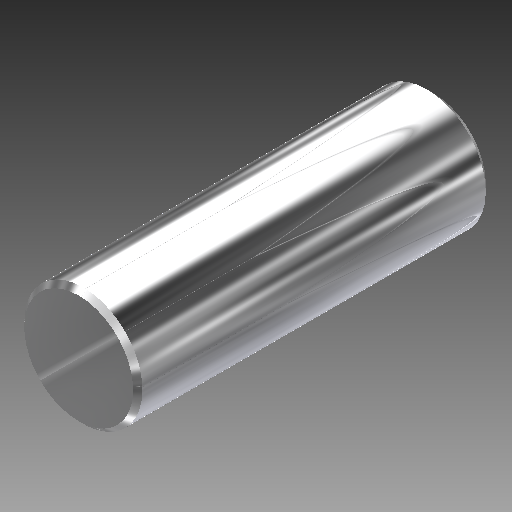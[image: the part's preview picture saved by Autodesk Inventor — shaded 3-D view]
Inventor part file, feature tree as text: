
AUTODESK INVENTOR PART (.ipt)
format: ipt  version: 2017 (Build 210142000, 142)  size: 182,784 bytes
history: native  units: in
note: dims shown in document units (in); Inventor stores cm internally (conversion verified against a paired STEP export)
features: other x35, revolve x1, sketch x1
ambient origin geometry x8: Origin, YZ Plane, XZ Plane, XY Plane, X Axis, Y Axis, Z Axis, Center Point
bodies: Solid1 (feature_tree)
feature tree (37):
  revolve  "Revolution1"  [1 undecoded]
  other  "dia1_XY"
  other  "dia1_YZ"
  other  "dia1_ZX"
  other  "dia1_X"
  other  "dia1_Y"
  other  "dia1_Z"
  other  "dia1_Center"
  other  "dia2_XY"
  other  "dia2_YZ"
  other  "dia2_ZX"
  other  "dia2_X"
  other  "dia2_Y"
  other  "dia2_Z"
  other  "dia2_Center"
  other  "pin_XY"
  other  "pin_YZ"
  other  "pin_ZX"
  other  "pin_X"
  other  "pin_Y"
  other  "pin_Z"
  other  "pin_Center"
  other  "pin1_XY"
  other  "pin1_YZ"
  other  "pin1_ZX"
  other  "pin1_X"
  other  "pin1_Y"
  other  "pin1_Z"
  other  "pin1_Center"
  other  "pin2_XY"
  other  "pin2_YZ"
  other  "pin2_ZX"
  other  "pin2_X"
  other  "pin2_Y"
  other  "pin2_Z"
  other  "pin2_Center"
  sketch  "Sketch_1"  dims[d0=360.0deg]
note: 1 required parameter value undecoded (feature->parameter linkage not recoverable at this tier; creation-order binding heuristic only, values carry confidence <= 0.55)
